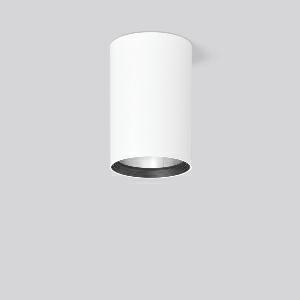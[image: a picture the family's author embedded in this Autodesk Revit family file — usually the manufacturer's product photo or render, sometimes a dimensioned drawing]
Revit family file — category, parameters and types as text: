
# Revit family: heledon_maxi_a_931218_002_f2bb
name_source: partatom
category: Lighting Fixtures
units: mm (PartAtom-declared; Revit-internal decimal feet)

## family parameters
Cut with Voids When Loaded = No
Host = Face
Light Source = No
Part Type = Normal
Room Calculation Point = No
Round Connector Dimension = Use Diameter
Shared = No

## types (1)
- HELEDON maxi A (1 x LED Modul 930, 3350 lm, 3000)
    Apparent Load = 25 VA
    Approval mark = CE
    CIE Flux Codes = 100 100 100 100 100
    Color Rendering = 90
    Color Temperature = 3000
    Default Elevation = 1800 mm
    Description = Series: HELEDON maxi
Cylindrical surface-mounted downlight. Housing: die-cast aluminium, powder-coated. Internal ceiling frame polycarbonate with bayonet mounting. Black plastic ring and recessed LED to prevent glare from the side. Optical assembly with reflector made of MIRO-Silver with 98% total light reflection for outstanding efficiency - can be changed without tools. Best colour rendering index Ra>90. Suitable for Ceiling mounting. Easy installation with a separate ceiling frame with bayonet mounting and plug connection. Driver integrated. Connected via plug-in connector. High quality converter without flickering and stroboscopic effect. The following accessories can be mounted without use of tools: interchangeable lenses, decorative glasses, honeycomb louvre, clear and frosted diffusers, white interchangeable plastic ring. 
Colour: traffic white, matt (RAL 9016)
Diameter: 123 mm
Height: 183 mm
Lamp: LED
Socket: without socket
Colour temperature: 3000K
Colour rendering index (CRI): 92
System power: 25 W
Rated luminous flux: 3350 lm
Luminous efficiency: 134 lm/W
Control gear: Regulated power supply
Protection class: I
Type of protection: IP 20
    Height = 183 mm
    Lamp = 1 x LED Modul 930
    Lamp Light Flux = 3350 lm
    Lamp count = 1
    Length = 123 mm
    Lifetime = 50000 h
    Luminous efficacy = 134 lm/W
    Manufacturer = RZB
    ModVariant = No
    Model = 931218.002
    Mounting Place = Ceiling
    Mounting Type = Surface mounted
    Number of Poles = 1
    OnlyDefault = Yes
    Power Factor = 1
    Product Name = HELEDON maxi A
    Product group = Surface mounted downlights
    ProductGroupID = 302
    Protection Class = Protection class I
    Protection Degree = IP 20
    RLX_Detail_Level = 1
    RLX_Emergency_Light_Flux = 0 lm
    RLX_Emergency_Type = 0
    RLX_Emergency_Type_DB = No
    RlxData = <blob elided: 98325 chars, md5=2628c975>
    Socket = socket
    Standby Power = 0 W
    System Light Flux = 3350 lm
    System Power = 25 W
    Type Comments = Product without accessories
    Type Image = 931192.002.jpg
    URL = http://relux.com
    VarID = ---
    Voltage = 230 V
    Voltage Range = 220-240 V
    Weight = 0.00 kg
    Width = 0 mm  [stored 0 ft]

note: [stored X ft] marks values corroborated as IEEE doubles in the binary element streams (Revit-internal decimal feet)

## geometry (parser evidence)
native form markers: Blend x4, Sweep x10
no freeform markers — native parametric forms only
